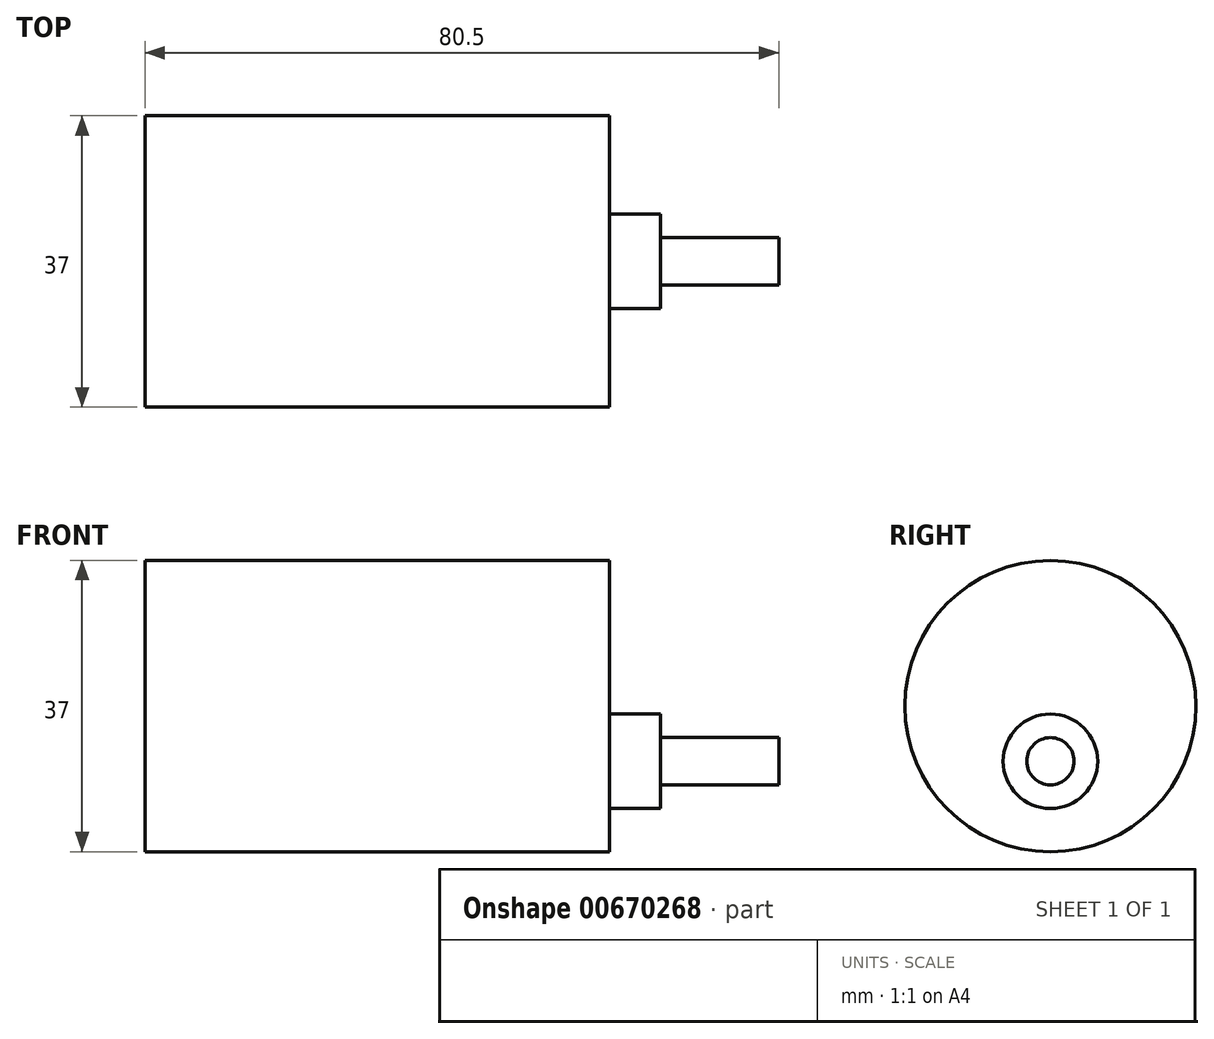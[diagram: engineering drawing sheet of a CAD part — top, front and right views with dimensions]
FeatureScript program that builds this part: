
annotation { "Feature Type Name" : "Feature", "Feature Type Description" : "" }
export const myFeature = defineFeature(function(context is Context, id is Id, definition is map)
    precondition{}
    {
        {
            var Q0;
            Q0=qCreatedBy(makeId("Right.planeOp"),FACE);
            var sketch = newSketch(context, id + "F0", { "sketchPlane" : qUnion([Q0])});
            skCircle(sketch, "E0", {"center": v(0, 0) * mm, "radius": 18.5 * mm});
            skSolve(sketch);
        }
        {
            var Q0;
            Q0=makeQuery(id+"F0.imprint","IMPRINT",FACE,{"disambiguationData":[TD([[makeQuery(id+"F0.imprint","IMPRINT",EDGE,{"derivedFrom":sQuery(id+"F0.wireOp",EDGE,"E0")}),1.0]])]});
            extrude(context, id + "F1", {"entities" : qUnion([Q0]), "depth" : -59 * mm, "offsetDistance" : 25 * mm});
        }
        {
            var Q0;
            Q0=makeQuery(id+"F1.opExtrude","CAP_FACE",FACE,{"disambiguationData":[OSD([sQuery(id+"F0.wireOp",EDGE,"E0")])],"isStart":true});
            var sketch = newSketch(context, id + "F2", { "sketchPlane" : qUnion([Q0])});
            skCircle(sketch, "E1", {"center": v(0, -7) * mm, "radius": 6 * mm});
            skSolve(sketch);
        }
        {
            var Q0;
            Q0=makeQuery(id+"F2.imprint","IMPRINT",FACE,{"disambiguationData":[TD([[makeQuery(id+"F2.imprint","IMPRINT",EDGE,{"derivedFrom":sQuery(id+"F2.wireOp",EDGE,"E1")}),1.0]])]});
            extrude(context, id + "F3", {"entities" : qUnion([Q0]), "operationType" : NewBodyOperationType.ADD, "depth" : 6.5 * mm, "offsetDistance" : 25 * mm});
        }
        {
            var Q0;
            Q0=makeQuery(id+"F3.opExtrude","CAP_FACE",FACE,{"disambiguationData":[OSD([sQuery(id+"F2.wireOp",EDGE,"E1")])],"isStart":false});
            var sketch = newSketch(context, id + "F4", { "sketchPlane" : qUnion([Q0])});
            skCircle(sketch, "E2", {"center": v(0, -7) * mm, "radius": 3 * mm});
            skSolve(sketch);
        }
        {
            var Q0;
            Q0=makeQuery(id+"F4.imprint","IMPRINT",FACE,{"disambiguationData":[TD([[makeQuery(id+"F4.imprint","IMPRINT",EDGE,{"derivedFrom":sQuery(id+"F4.wireOp",EDGE,"E2")}),1.0]])]});
            extrude(context, id + "F5", {"entities" : qUnion([Q0]), "operationType" : NewBodyOperationType.ADD, "depth" : 15 * mm, "offsetDistance" : 25 * mm});
        }
    });
